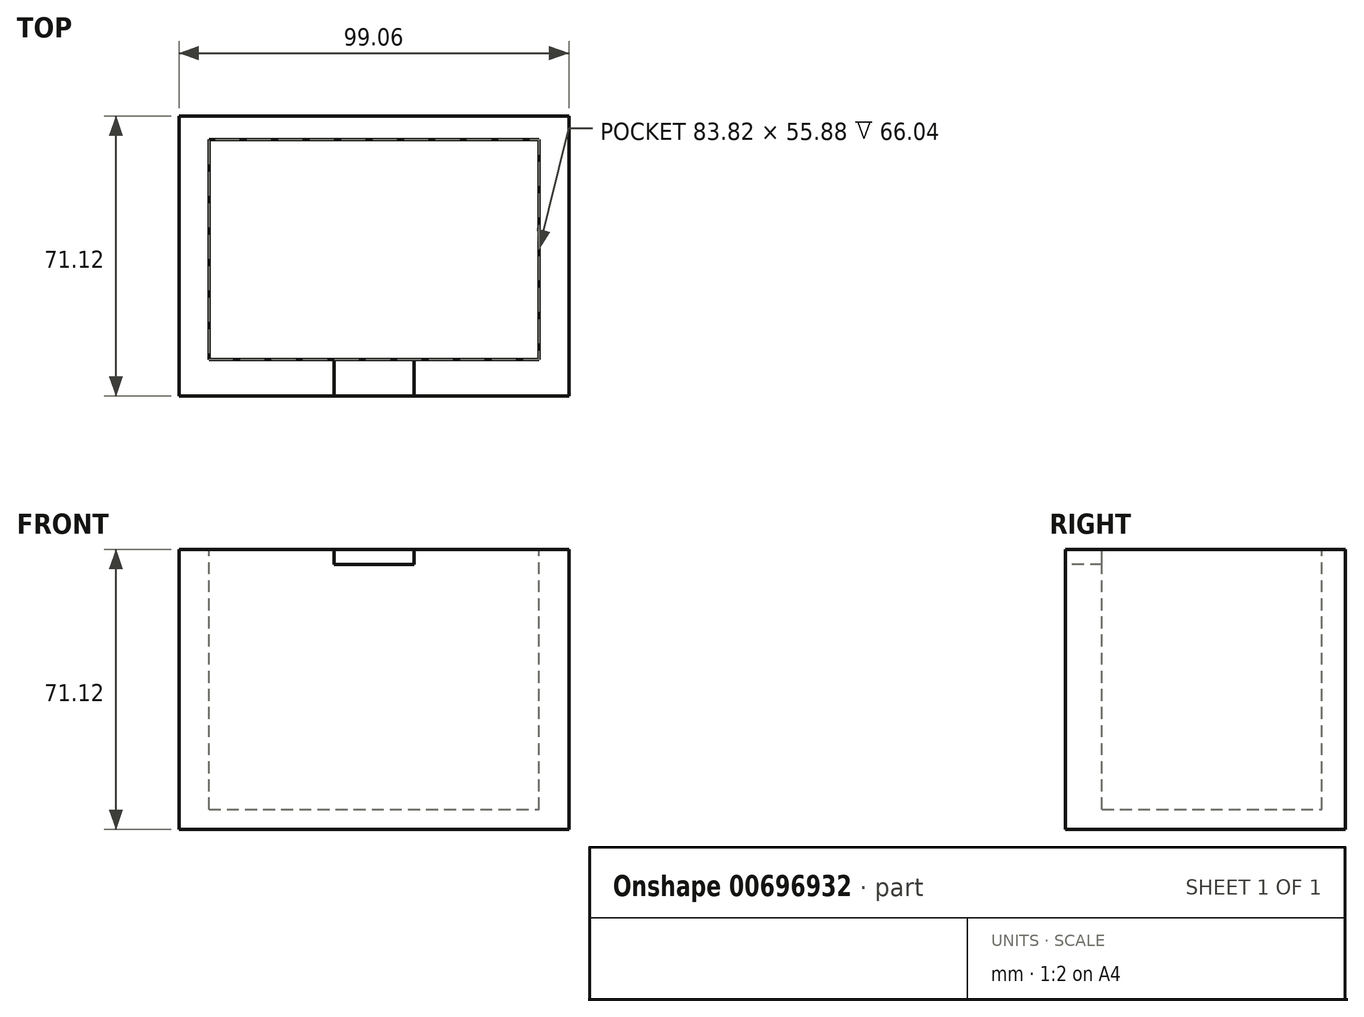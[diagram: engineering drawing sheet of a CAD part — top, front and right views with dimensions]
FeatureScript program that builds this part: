
annotation { "Feature Type Name" : "Feature", "Feature Type Description" : "" }
export const myFeature = defineFeature(function(context is Context, id is Id, definition is map)
    precondition{}
    {
        {
            var Q0;
            Q0=qCreatedBy(makeId("Top.planeOp"),FACE);
            var sketch = newSketch(context, id + "F0", { "sketchPlane" : qUnion([Q0])});
            skLineSegment(sketch, "E0.bottom", {"start": v(-49.53, 33.86) * mm, "end": v(49.53, 33.86) * mm});
            skLineSegment(sketch, "E0.top", {"start": v(-49.53, -37.26) * mm, "end": v(49.53, -37.26) * mm});
            skLineSegment(sketch, "E0.left", {"start": v(-49.53, 33.86) * mm, "end": v(-49.53, -37.26) * mm});
            skLineSegment(sketch, "E0.right", {"start": v(49.53, 33.86) * mm, "end": v(49.53, -37.26) * mm});
            skPoint(sketch, "E0.middle", {"position": v(0, -1.7) * mm});
            skSolve(sketch);
        }
        {
            var Q0;
            Q0=makeQuery(id+"F0.imprint","IMPRINT",FACE,{"disambiguationData":[TD([[makeQuery(id+"F0.imprint","IMPRINT",EDGE,{"derivedFrom":sQuery(id+"F0.wireOp",EDGE,"E0.bottom")}),-1.0]])]});
            extrude(context, id + "F1", {"entities" : qUnion([Q0]), "depth" : 71.12 * mm, "offsetDistance" : 25.4 * mm});
        }
        {
            var Q0;
            Q0=makeQuery(id+"F1.opExtrude","CAP_FACE",FACE,{"disambiguationData":[OSD([sQuery(id+"F0.wireOp",EDGE,"E0.bottom"),sQuery(id+"F0.wireOp",EDGE,"E0.top"),sQuery(id+"F0.wireOp",EDGE,"E0.left"),sQuery(id+"F0.wireOp",EDGE,"E0.right")])],"isStart":false});
            var sketch = newSketch(context, id + "F2", { "sketchPlane" : qUnion([Q0])});
            skLineSegment(sketch, "E1.bottom", {"start": v(0, 0) * mm, "end": v(-41.91, 0) * mm});
            skLineSegment(sketch, "E1.top", {"start": v(0, 27.94) * mm, "end": v(-41.91, 27.94) * mm});
            skLineSegment(sketch, "E1.left", {"start": v(0, 0) * mm, "end": v(0, 27.94) * mm});
            skLineSegment(sketch, "E1.right", {"start": v(-41.91, 0) * mm, "end": v(-41.91, 27.94) * mm});
            skLineSegment(sketch, "E2.bottom", {"start": v(0, 0) * mm, "end": v(41.91, 0) * mm});
            skLineSegment(sketch, "E2.top", {"start": v(0, 27.94) * mm, "end": v(41.91, 27.94) * mm});
            skLineSegment(sketch, "E2.right", {"start": v(41.91, 0) * mm, "end": v(41.91, 27.94) * mm});
            skLineSegment(sketch, "E3.top", {"start": v(0, -27.94) * mm, "end": v(-41.9, -27.94) * mm});
            skLineSegment(sketch, "E3.left", {"start": v(0, 0) * mm, "end": v(0, -27.94) * mm});
            skLineSegment(sketch, "E3.right", {"start": v(-41.91, 0) * mm, "end": v(-41.9, -27.94) * mm});
            skLineSegment(sketch, "E4.top", {"start": v(0, -27.94) * mm, "end": v(41.91, -27.94) * mm});
            skLineSegment(sketch, "E4.right", {"start": v(41.91, 0) * mm, "end": v(41.91, -27.94) * mm});
            skSolve(sketch);
        }
        {
            var Q0;
            Q0=makeQuery(id+"F2.imprint","IMPRINT",FACE,{"disambiguationData":[TD([[makeQuery(id+"F2.imprint","IMPRINT",EDGE,{"derivedFrom":sQuery(id+"F2.wireOp",EDGE,"E1.top")}),1.0]])]});
            var Q1;
            Q1=makeQuery(id+"F2.imprint","IMPRINT",FACE,{"disambiguationData":[TD([[makeQuery(id+"F2.imprint","IMPRINT",EDGE,{"derivedFrom":sQuery(id+"F2.wireOp",EDGE,"E2.top")}),-1.0]])]});
            var Q2;
            Q2=makeQuery(id+"F2.imprint","IMPRINT",FACE,{"disambiguationData":[TD([[makeQuery(id+"F2.imprint","IMPRINT",EDGE,{"derivedFrom":sQuery(id+"F2.wireOp",EDGE,"E2.bottom")}),-1.0]])]});
            var Q3;
            Q3=makeQuery(id+"F2.imprint","IMPRINT",FACE,{"disambiguationData":[TD([[makeQuery(id+"F2.imprint","IMPRINT",EDGE,{"derivedFrom":sQuery(id+"F2.wireOp",EDGE,"E1.bottom")}),1.0]])]});
            extrude(context, id + "F3", {"entities" : qUnion([Q0, Q1, Q2, Q3]), "operationType" : NewBodyOperationType.REMOVE, "oppositeDirection" : true, "depth" : 66.04 * mm, "offsetDistance" : 25.4 * mm});
        }
        {
            var Q0;
            Q0=makeQuery(id+"F1.opExtrude","SWEPT_FACE",FACE,{"disambiguationData":[OSD([sQuery(id+"F0.wireOp",EDGE,"E0.top")])]});
            var sketch = newSketch(context, id + "F4", { "sketchPlane" : qUnion([Q0])});
            skLineSegment(sketch, "E5.bottom", {"start": v(-10.16, 67.31) * mm, "end": v(10.16, 67.31) * mm});
            skLineSegment(sketch, "E5.top", {"start": v(-10.16, 74.93) * mm, "end": v(10.16, 74.93) * mm});
            skLineSegment(sketch, "E5.left", {"start": v(-10.16, 67.31) * mm, "end": v(-10.16, 74.93) * mm});
            skLineSegment(sketch, "E5.right", {"start": v(10.16, 67.31) * mm, "end": v(10.16, 74.93) * mm});
            skPoint(sketch, "E5.middle", {"position": v(0, 71.12) * mm});
            skSolve(sketch);
        }
        {
            var Q0;
            {var subQ0=sQuery(id+"F4.wireOp",EDGE,"E5.bottom");Q0=makeQuery(id+"F4.imprint","IMPRINT",FACE,{"disambiguationData":[TD([[makeQuery(id+"F4.imprint","IMPRINT",EDGE,{"derivedFrom":subQ0}),1.0]])]});}
            extrude(context, id + "F5", {"entities" : qUnion([Q0]), "operationType" : NewBodyOperationType.REMOVE, "oppositeDirection" : true, "depth" : 10.16 * mm, "offsetDistance" : 25.4 * mm});
        }
    });
